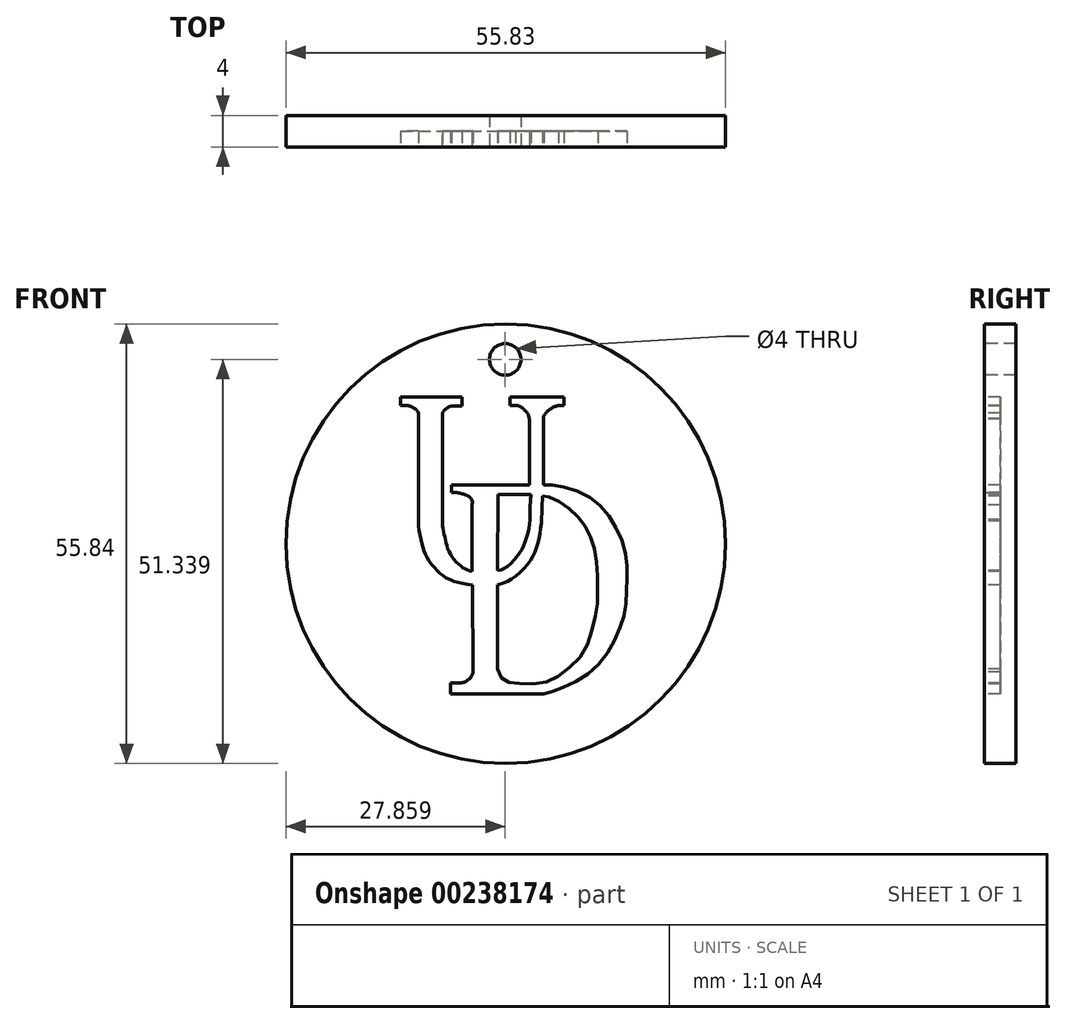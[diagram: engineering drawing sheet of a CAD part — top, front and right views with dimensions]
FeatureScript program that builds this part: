
annotation { "Feature Type Name" : "Feature", "Feature Type Description" : "" }
export const myFeature = defineFeature(function(context is Context, id is Id, definition is map)
    precondition{}
    {
        {
            var Q0;
            Q0=qCreatedBy(makeId("Front.planeOp"),FACE);
            var sketch = newSketch(context, id + "F0", { "sketchPlane" : qUnion([Q0])});
            skPoint(sketch, "E0", {"position": v(34.43, 29.34) * mm});
            skLineSegment(sketch, "E1", {"start": v(21.24, 48) * mm, "end": v(28.87, 48) * mm});
            skLineSegment(sketch, "E2", {"start": v(28.87, 48) * mm, "end": v(28.87, 46.84) * mm});
            skLineSegment(sketch, "E3", {"start": v(21.1, 46.91) * mm, "end": v(21.1, 48) * mm});
            skLineSegment(sketch, "E4", {"start": v(21.24, 48) * mm, "end": v(21.1, 48) * mm});
            skLineSegment(sketch, "E5", {"start": v(21.1, 46.91) * mm, "end": v(21.68, 46.91) * mm});
            skLineSegment(sketch, "E6", {"start": v(28.87, 46.84) * mm, "end": v(27.84, 46.84) * mm});
            skArc(sketch, "E7", {"start": v(23.38, 45.98) * mm, "mid": v(22.65, 46.66) * mm, "end": v(21.68, 46.91) * mm});
            skArc(sketch, "E8", {"start": v(27.84, 46.84) * mm, "mid": v(27, 46.6) * mm, "end": v(26.42, 45.98) * mm});
            skLineSegment(sketch, "E9", {"start": v(23.38, 45.98) * mm, "end": v(23.38, 32.26) * mm});
            skLineSegment(sketch, "E10", {"start": v(26.42, 45.98) * mm, "end": v(26.42, 32.4) * mm});
            skLineSegment(sketch, "E11", {"start": v(30.15, 25.82) * mm, "end": v(30.15, 34.24) * mm});
            skLineSegment(sketch, "E12", {"start": v(27.56, 35.83) * mm, "end": v(27.56, 36.8) * mm});
            skLineSegment(sketch, "E13", {"start": v(27.56, 36.8) * mm, "end": v(37.44, 36.8) * mm});
            skLineSegment(sketch, "E14", {"start": v(37.44, 36.8) * mm, "end": v(37.44, 45.18) * mm});
            skFitSpline(sketch, "E15", {"points": [v(23.38, 32.26) * mm, v(23.38, 31.52) * mm, v(23.7, 29.74) * mm, v(24.08, 28.4) * mm, v(24.63, 27.27) * mm, v(25.64, 26.03) * mm, v(26.67, 25.15) * mm, v(28.18, 24.47) * mm, v(30.24, 24.11) * mm], "startDerivative": vector(-0.45, -7.25) * mm, "endDerivative": vector(14.24, -1.73) * mm});
            skLineSegment(sketch, "E16", {"start": v(30.3, 13.09) * mm, "end": v(30.24, 24.11) * mm});
            skLineSegment(sketch, "E17", {"start": v(33.38, 13.44) * mm, "end": v(33.38, 24.11) * mm});
            skFitSpline(sketch, "E18", {"points": [v(30.3, 13.09) * mm, v(30.1, 12.48) * mm, v(29.74, 12.12) * mm, v(29.12, 11.74) * mm, v(28.45, 11.69) * mm, v(27.46, 11.68) * mm], "startDerivative": vector(-0.86, -3.46) * mm, "endDerivative": vector(-4.38, -0.1) * mm});
            skLineSegment(sketch, "E19", {"start": v(27.46, 11.68) * mm, "end": v(27.46, 10.24) * mm});
            skLineSegment(sketch, "E20", {"start": v(35, 46.93) * mm, "end": v(35, 48) * mm});
            skLineSegment(sketch, "E21", {"start": v(35, 48) * mm, "end": v(41.83, 48) * mm});
            skLineSegment(sketch, "E22", {"start": v(41.83, 48) * mm, "end": v(41.83, 46.9) * mm});
            skLineSegment(sketch, "E23", {"start": v(41.83, 46.9) * mm, "end": v(41.14, 46.9) * mm});
            skLineSegment(sketch, "E24", {"start": v(35, 46.93) * mm, "end": v(35.7, 46.93) * mm});
            skFitSpline(sketch, "E25", {"points": [v(35.7, 46.93) * mm, v(35.92, 46.93) * mm, v(36.32, 46.75) * mm, v(36.7, 46.45) * mm, v(37, 46.16) * mm, v(37.3, 45.74) * mm, v(37.44, 45.18) * mm], "startDerivative": vector(1.68, 0.2) * mm, "endDerivative": vector(0.53, -3.05) * mm});
            skLineSegment(sketch, "E26", {"start": v(39.24, 36.83) * mm, "end": v(39.24, 45.27) * mm});
            skFitSpline(sketch, "E27", {"points": [v(39.24, 45.27) * mm, v(39.24, 45.5) * mm, v(39.5, 45.88) * mm, v(39.97, 46.38) * mm, v(40.8, 46.8) * mm, v(41.14, 46.9) * mm], "startDerivative": vector(-0.29, 1.64) * mm, "endDerivative": vector(1.76, 0.4) * mm});
            skLineSegment(sketch, "E28", {"start": v(37.45, 35.58) * mm, "end": v(33.45, 35.58) * mm});
            skLineSegment(sketch, "E29", {"start": v(33.42, 25.94) * mm, "end": v(33.45, 35.58) * mm});
            skFitSpline(sketch, "E30", {"points": [v(26.42, 32.4) * mm, v(26.42, 31.57) * mm, v(26.7, 30.17) * mm, v(27.09, 28.72) * mm, v(28.02, 27.16) * mm, v(29.27, 26.15) * mm, v(30.15, 25.82) * mm], "startDerivative": vector(-0.38, -5.91) * mm, "endDerivative": vector(6.08, -1.82) * mm});
            skFitSpline(sketch, "E31", {"points": [v(30.15, 34.24) * mm, v(30.15, 34.86) * mm, v(29.58, 35.46) * mm, v(29, 35.68) * mm, v(28.1, 35.85) * mm, v(27.56, 35.83) * mm], "startDerivative": vector(0.64, 3.3) * mm, "endDerivative": vector(-2.77, -0.27) * mm});
            skFitSpline(sketch, "E32", {"points": [v(33.42, 25.94) * mm, v(34.54, 26.36) * mm, v(36.03, 27.93) * mm, v(36.83, 29.32) * mm, v(37.43, 31.46) * mm, v(37.52, 33.01) * mm, v(37.54, 34.24) * mm, v(37.62, 35.3) * mm, v(37.65, 35.58) * mm], "startDerivative": vector(9.28, 2.05) * mm, "endDerivative": vector(0.5, 4) * mm});
            skLineSegment(sketch, "E33", {"start": v(37.45, 35.58) * mm, "end": v(37.65, 35.58) * mm});
            skFitSpline(sketch, "E34", {"points": [v(33.38, 24.11) * mm, v(34.4, 24.44) * mm, v(36.3, 25.71) * mm, v(37.81, 27.6) * mm, v(38.52, 29.41) * mm, v(38.94, 31.71) * mm, v(39.07, 33.93) * mm, v(39.1, 35.4) * mm], "startDerivative": vector(8.86, 2.18) * mm, "endDerivative": vector(0.17, 11.19) * mm});
            skFitSpline(sketch, "E35", {"points": [v(39.1, 35.4) * mm, v(39.6, 35.4) * mm, v(40.77, 34.93) * mm, v(42.44, 33.86) * mm, v(43.88, 32.48) * mm, v(44.85, 31) * mm, v(45.6, 29.1) * mm, v(46.02, 26.8) * mm, v(46.08, 24.11) * mm, v(46.11, 21.7) * mm, v(45.7, 19.5) * mm, v(44.77, 16.45) * mm, v(43.16, 14.15) * mm, v(40.9, 12.42) * mm, v(38.88, 11.6) * mm, v(36.33, 11.6) * mm, v(34.88, 11.72) * mm, v(33.91, 12.28) * mm, v(33.38, 13.44) * mm], "startDerivative": vector(16.18, 1.81) * mm, "endDerivative": vector(-9.26, 28.4) * mm});
            skFitSpline(sketch, "E36", {"points": [v(39.3, 10.24) * mm, v(40.89, 10.78) * mm, v(44.1, 12.25) * mm, v(46.98, 14.9) * mm, v(48.82, 18.34) * mm, v(49.65, 21.21) * mm, v(49.8, 24.26) * mm, v(49.8, 27.2) * mm, v(48.87, 30.54) * mm, v(46.95, 33.64) * mm, v(44.2, 35.76) * mm, v(40.71, 36.76) * mm, v(39.24, 36.83) * mm], "startDerivative": vector(23.51, 7.52) * mm, "endDerivative": vector(-22.5, -0.2) * mm});
            skLineSegment(sketch, "E37", {"start": v(27.46, 10.24) * mm, "end": v(39.3, 10.24) * mm});
            skSolve(sketch);
        }
        {
            var Q0;
            Q0=qCreatedBy(makeId("Front.planeOp"),FACE);
            var sketch = newSketch(context, id + "F1", { "sketchPlane" : qUnion([Q0])});
            skCircle(sketch, "E38", {"center": v(34.44, 29.34) * mm, "radius": 27.92 * mm});
            skSolve(sketch);
        }
        {
            var Q0;
            Q0 = qSketchRegion(id + "F1", true);
            extrude(context, id + "F2", {"entities" : qUnion([Q0]), "oppositeDirection" : true, "depth" : 4 * mm, "offsetDistance" : 25 * mm});
        }
        {
            var Q0;
            Q0 = qSketchRegion(id + "F0", true);
            extrude(context, id + "F3", {"entities" : qUnion([Q0]), "operationType" : NewBodyOperationType.REMOVE, "oppositeDirection" : true, "depth" : 2 * mm, "offsetDistance" : 25 * mm});
        }
        {
            var Q0;
            {var subQ0=sQuery(id+"F1.wireOp",EDGE,"E38");Q0=makeQuery(id+"F3.boolean.opBoolean","SPLIT",FACE,{"disambiguationData":[TD([makeQuery(id+"F2.opExtrude","SWEPT_FACE",FACE,{"disambiguationData":[OSD([subQ0])]})])],"derivedFrom":makeQuery(id+"F2.opExtrude","CAP_FACE",FACE,{"disambiguationData":[OSD([subQ0])],"isStart":true})});}
            var sketch = newSketch(context, id + "F4", { "sketchPlane" : qUnion([Q0])});
            skPoint(sketch, "E39", {"position": v(34.38, 57.26) * mm});
            skCircle(sketch, "E40", {"center": v(34.38, 52.76) * mm, "radius": 2 * mm});
            skSolve(sketch);
        }
        {
            var Q0;
            Q0 = qSketchRegion(id + "F4", true);
            extrude(context, id + "F5", {"entities" : qUnion([Q0]), "operationType" : NewBodyOperationType.REMOVE, "oppositeDirection" : true, "depth" : 25 * mm, "offsetDistance" : 25 * mm});
        }
    });
